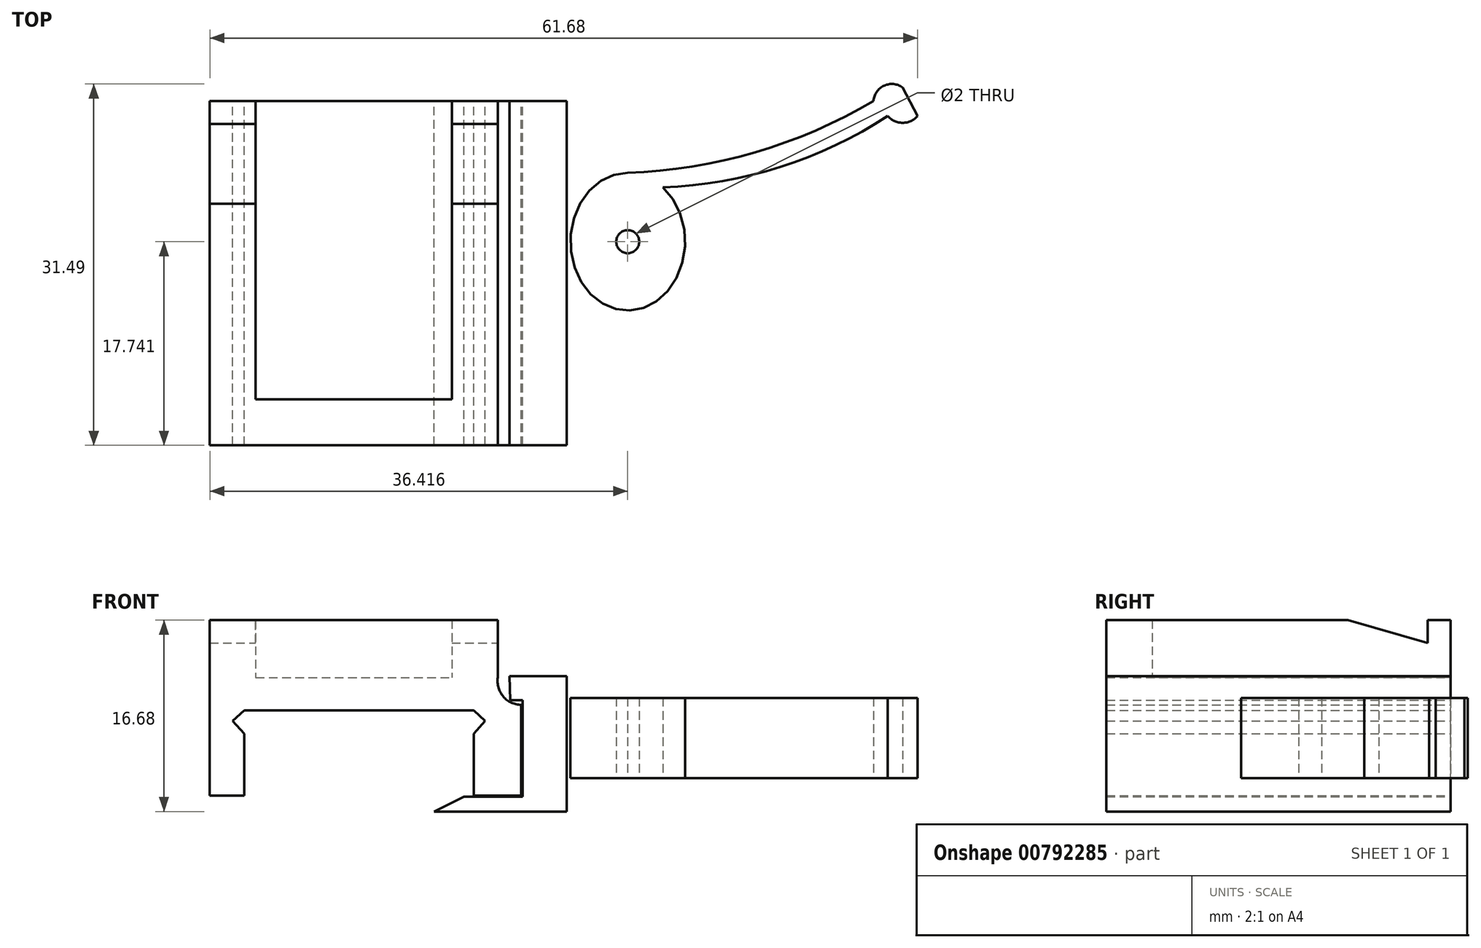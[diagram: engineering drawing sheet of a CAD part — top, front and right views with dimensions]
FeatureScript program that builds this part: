
annotation { "Feature Type Name" : "Feature", "Feature Type Description" : "" }
export const myFeature = defineFeature(function(context is Context, id is Id, definition is map)
    precondition{}
    {
        {
            var Q0;
            Q0=qCreatedBy(makeId("Front.planeOp"),FACE);
            var sketch = newSketch(context, id + "F0", { "sketchPlane" : qUnion([Q0])});
            skLineSegment(sketch, "E0", {"start": v(0, 17.85) * mm, "end": v(0, -18.14) * mm, "construction": true});
            skLineSegment(sketch, "E1.bottom", {"start": v(-10.24, 3.78) * mm, "end": v(14.85, 3.78) * mm});
            skLineSegment(sketch, "E1.top", {"start": v(-10.24, -6.5) * mm, "end": v(-7.24, -6.5) * mm});
            skLineSegment(sketch, "E1.left", {"start": v(-10.24, 3.78) * mm, "end": v(-10.24, -6.5) * mm});
            skLineSegment(sketch, "E1.right", {"start": v(14.85, 3.78) * mm, "end": v(14.85, 3.15) * mm});
            skLineSegment(sketch, "E2", {"start": v(-7.24, -6.5) * mm, "end": v(-7.24, -1.11) * mm});
            skLineSegment(sketch, "E3", {"start": v(-7.24, -1.11) * mm, "end": v(-8.24, 0) * mm});
            skLineSegment(sketch, "E4", {"start": v(-8.24, 0) * mm, "end": v(-7.24, 0.9) * mm});
            skLineSegment(sketch, "E5", {"start": v(-7.24, 0.9) * mm, "end": v(12.76, 0.9) * mm});
            skLineSegment(sketch, "E6", {"start": v(12.76, 0.9) * mm, "end": v(13.76, 0) * mm});
            skLineSegment(sketch, "E7", {"start": v(13.76, 0) * mm, "end": v(12.76, -1.11) * mm});
            skLineSegment(sketch, "E8", {"start": v(12.76, -1.11) * mm, "end": v(12.76, -6.5) * mm});
            skLineSegment(sketch, "E9", {"start": v(-7.24, -1.11) * mm, "end": v(12.76, -1.11) * mm, "construction": true});
            skLineSegment(sketch, "E10.right", {"start": v(16.9, -6.5) * mm, "end": v(16.9, 1.4) * mm});
            skArc(sketch, "E11", {"start": v(14.85, 3.78) * mm, "mid": v(15.33, 2.12) * mm, "end": v(16.9, 1.4) * mm});
            skLineSegment(sketch, "E12", {"start": v(16.9, -6.5) * mm, "end": v(12.76, -6.5) * mm});
            skLineSegment(sketch, "E13", {"start": v(9.3, -7.9) * mm, "end": v(20.87, -7.9) * mm});
            skLineSegment(sketch, "E14", {"start": v(20.87, -7.9) * mm, "end": v(20.87, 3.91) * mm});
            skLineSegment(sketch, "E15", {"start": v(20.87, 3.91) * mm, "end": v(15.87, 3.91) * mm});
            skLineSegment(sketch, "E16", {"start": v(9.3, -7.9) * mm, "end": v(11.9, -6.6) * mm});
            skLineSegment(sketch, "E17", {"start": v(11.9, -6.6) * mm, "end": v(17.03, -6.6) * mm});
            skLineSegment(sketch, "E18", {"start": v(17.03, -6.6) * mm, "end": v(17.03, 1.81) * mm});
            skLineSegment(sketch, "E19", {"start": v(17.03, 1.81) * mm, "end": v(15.93, 1.81) * mm});
            skLineSegment(sketch, "E20", {"start": v(15.93, 1.81) * mm, "end": v(15.87, 3.91) * mm});
            skSolve(sketch);
        }
        {
            var Q0;
            {var subQ0=sQuery(id+"F0.wireOp",EDGE,"E1.bottom");Q0=makeQuery(id+"F0.imprint","IMPRINT",FACE,{"disambiguationData":[TD([[makeQuery(id+"F0.imprint","IMPRINT",EDGE,{"derivedFrom":subQ0}),-1.0]])]});}
            var Q1;
            Q1=makeQuery(id+"F0.imprint","IMPRINT",FACE,{"disambiguationData":[TD([[makeQuery(id+"F0.imprint","IMPRINT",EDGE,{"derivedFrom":sQuery(id+"F0.wireOp",EDGE,"E13")}),1.0]])]});
            extrude(context, id + "F1", {"entities" : qUnion([Q0, Q1]), "depth" : 30 * mm, "offsetDistance" : 25 * mm});
        }
        {
            var Q0;
            Q0=qCreatedBy(makeId("Top.planeOp"),FACE);
            var sketch = newSketch(context, id + "F2", { "sketchPlane" : qUnion([Q0])});
            skEllipticalArc(sketch, "E21", {});
            skArc(sketch, "E22", {"start": v(26.18, -6.26) * mm, "mid": v(37.27, -4.47) * mm, "end": v(47.59, 0) * mm});
            skArc(sketch, "E23", {"start": v(48.83, -1.3) * mm, "mid": v(50.14, -1.9) * mm, "end": v(51.44, -1.3) * mm});
            skArc(sketch, "E24", {"start": v(50.14, 1.18) * mm, "mid": v(48.52, 1.34) * mm, "end": v(47.59, 0) * mm});
            skLineSegment(sketch, "E25", {"start": v(50.14, 1.18) * mm, "end": v(51.44, -1.3) * mm});
            skCircle(sketch, "E26", {"center": v(26.18, -12.26) * mm, "radius": 1 * mm});
            skArc(sketch, "E27", {"start": v(29.25, -7.53) * mm, "mid": v(39.46, -5.75) * mm, "end": v(48.83, -1.3) * mm});
            const initialGuessF2  = {"E21": [0.026176143437623978, -0.01225948054343462, 0, 1, 0.006, 0.005, 0, 5.621212582478396]};
            skSetInitialGuess(sketch, initialGuessF2);
            skSolve(sketch);
        }
        {
            var Q0;
            Q0=makeQuery(id+"F2.imprint","IMPRINT",FACE,{"disambiguationData":[TD([[makeQuery(id+"F2.imprint","IMPRINT",EDGE,{"derivedFrom":sQuery(id+"F2.wireOp",EDGE,"E21")}),1.0]])]});
            extrude(context, id + "F3", {"entities" : qUnion([Q0]), "depth" : 2 * mm, "offsetDistance" : 25 * mm, "hasSecondDirection" : true, "secondDirectionOppositeDirection" : true, "secondDirectionDepth" : 5 * mm});
        }
        {
            var Q0;
            Q0=makeQuery(id+"F1.opExtrude","SWEPT_FACE",FACE,{"disambiguationData":[OSD([sQuery(id+"F0.wireOp",EDGE,"E1.bottom")])]});
            var sketch = newSketch(context, id + "F4", { "sketchPlane" : qUnion([Q0])});
            skLineSegment(sketch, "E28.bottom", {"start": v(-10.24, 0) * mm, "end": v(-6.24, 0) * mm});
            skLineSegment(sketch, "E28.top", {"start": v(-10.24, -30) * mm, "end": v(-6.24, -30) * mm});
            skLineSegment(sketch, "E28.left", {"start": v(-10.24, 0) * mm, "end": v(-10.24, -30) * mm});
            skLineSegment(sketch, "E28.right", {"start": v(-6.24, 0) * mm, "end": v(-6.24, -26) * mm});
            skLineSegment(sketch, "E29.bottom", {"start": v(-6.24, -26) * mm, "end": v(10.85, -26) * mm});
            skLineSegment(sketch, "E29.top", {"start": v(-10.24, -30) * mm, "end": v(14.85, -30) * mm});
            skLineSegment(sketch, "E29.left", {"start": v(-10.24, -26) * mm, "end": v(-10.24, -30) * mm});
            skLineSegment(sketch, "E29.right", {"start": v(14.85, -26) * mm, "end": v(14.85, -30) * mm});
            skLineSegment(sketch, "E30.bottom", {"start": v(10.85, -30) * mm, "end": v(14.85, -30) * mm});
            skLineSegment(sketch, "E30.top", {"start": v(10.85, 0) * mm, "end": v(14.85, 0) * mm});
            skLineSegment(sketch, "E30.left", {"start": v(10.85, -26) * mm, "end": v(10.85, 0) * mm});
            skLineSegment(sketch, "E30.right", {"start": v(14.85, -30) * mm, "end": v(14.85, 0) * mm});
            skSolve(sketch);
        }
        {
            var Q0;
            Q0=makeQuery(id+"F4.imprint","IMPRINT",FACE,{"disambiguationData":[TD([[makeQuery(id+"F4.imprint","IMPRINT",EDGE,{"derivedFrom":sQuery(id+"F4.wireOp",EDGE,"E28.bottom")}),-1.0]])]});
            extrude(context, id + "F5", {"entities" : qUnion([Q0]), "operationType" : NewBodyOperationType.ADD, "depth" : 5 * mm, "offsetDistance" : 25 * mm});
        }
        {
            var Q0;
            Q0=makeQuery(id+"F5.opExtrude","SWEPT_FACE",FACE,{"disambiguationData":[OSD([sQuery(id+"F4.wireOp",EDGE,"E30.right")])]});
            var sketch = newSketch(context, id + "F6", { "sketchPlane" : qUnion([Q0])});
            skLineSegment(sketch, "E31.bottom", {"start": v(-2, 8.78) * mm, "end": v(-2.45, 8.78) * mm});
            skLineSegment(sketch, "E32", {"start": v(-2, 6.78) * mm, "end": v(-8.95, 8.78) * mm});
            skLineSegment(sketch, "E33", {"start": v(-8.95, 8.78) * mm, "end": v(-2.45, 8.78) * mm});
            skLineSegment(sketch, "E34", {"start": v(-2, 6.78) * mm, "end": v(-2, 8.78) * mm});
            skSolve(sketch);
        }
        {
            var Q0;
            Q0=makeQuery(id+"F6.imprint","IMPRINT",FACE,{"disambiguationData":[TD([[makeQuery(id+"F6.imprint","IMPRINT",EDGE,{"derivedFrom":sQuery(id+"F6.wireOp",EDGE,"E31.bottom")}),-1.0]])]});
            extrude(context, id + "F7", {"entities" : qUnion([Q0]), "operationType" : NewBodyOperationType.REMOVE, "oppositeDirection" : true, "depth" : 40 * mm, "offsetDistance" : 25 * mm, "hasSecondDirection" : true, "secondDirectionOppositeDirection" : false, "secondDirectionDepth" : 25 * mm});
        }
    });
